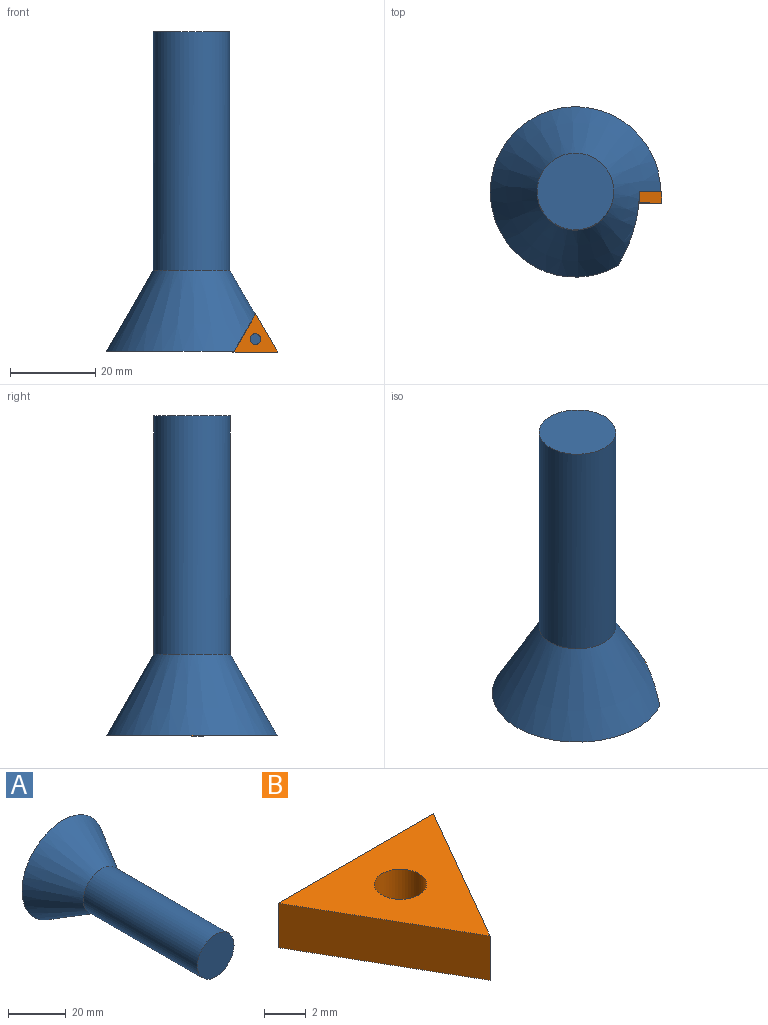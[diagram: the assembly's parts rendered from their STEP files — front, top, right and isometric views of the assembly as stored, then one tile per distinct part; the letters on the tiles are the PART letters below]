
ASSEMBLY  parts=2 mates=1
PART A: 6 faces, bbox 40x75x40 mm
  f0: cone r=20mm half-angle=30deg, axis (0,1,0), area 1874.1mm2, adj f1,f3,f4,f5
  f1: cylinder r=9mm len=55.95mm, axis (0,-1,0), area 3163.8mm2, adj f0,f2
  f2: plane 18x18mm, normal (0,-1,0), area 254.5mm2, adj f1
  f3: plane 40x40mm, normal (0,1,0), area 1133.8mm2, adj f0,f4,f5
  f4: plane 17.32x8.66mm, normal (0.87,0.5,0), area 115.5mm2, adj f0,f3,f5
  f5: plane 10x8.66mm, normal (0,0,-1), area 43.3mm2, adj f0,f3,f4
PART B: 6 faces, bbox 10.5x9.1x2.6 mm
  f0: plane 9.09x5.25mm, normal (0.87,-0.5,0), area 27.3mm2, adj f1,f2,f4,f5
  f1: plane 9.09x5.25mm, normal (-0.87,-0.5,0), area 27.3mm2, adj f0,f2,f4,f5
  f2: plane 10.5x2.6mm, normal (0,1,0), area 27.3mm2, adj f0,f1,f4,f5
  f3: cylinder r=1.25mm len=2.6mm, axis (0,0,-1), area 20.4mm2, adj f4,f5
  f4: plane 10.5x9.09mm, normal (0,0,1), area 42.8mm2, adj f0,f1,f2,f3
  f5: plane 10.5x9.09mm, normal (0,0,-1), area 42.8mm2, adj f0,f1,f2,f3
PLACE A rot(axis=(-1,0,0),90deg) t=(-2.63,-30.18,-47.28)mm
PLACE B rot(axis=(-1,0,0),90deg) t=(-2.83,-32.78,-47.24)mm
MATE fastened A.f5 <-> B.f3  axis (0,-1,0) through (12.37,-30.18,-44.4)mm
